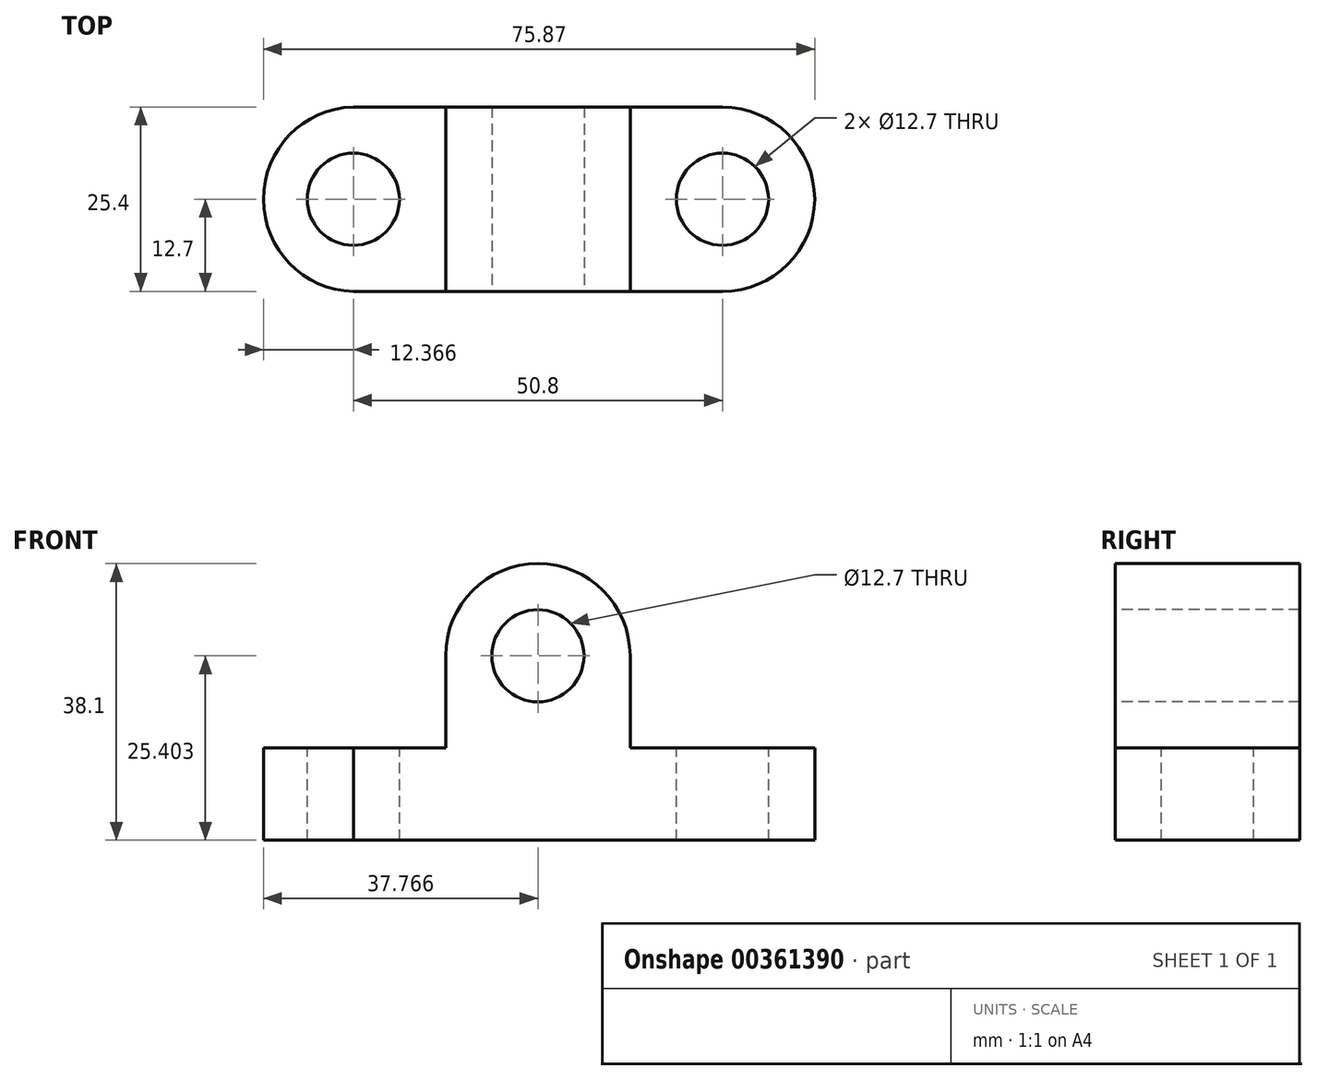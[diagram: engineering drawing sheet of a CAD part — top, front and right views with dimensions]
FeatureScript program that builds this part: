
annotation { "Feature Type Name" : "Feature", "Feature Type Description" : "" }
export const myFeature = defineFeature(function(context is Context, id is Id, definition is map)
    precondition{}
    {
        {
            var Q0;
            Q0=qCreatedBy(makeId("Front.planeOp"),FACE);
            var sketch = newSketch(context, id + "F0", { "sketchPlane" : qUnion([Q0])});
            skLineSegment(sketch, "E0", {"start": v(-39.1, 16.45) * mm, "end": v(-39.1, 3.75) * mm});
            skLineSegment(sketch, "E1", {"start": v(-39.1, 3.75) * mm, "end": v(37.1, 3.75) * mm});
            skLineSegment(sketch, "E2", {"start": v(37.1, 3.75) * mm, "end": v(37.1, 16.45) * mm});
            skLineSegment(sketch, "E3", {"start": v(37.1, 16.45) * mm, "end": v(11.7, 16.45) * mm});
            skLineSegment(sketch, "E4", {"start": v(11.7, 16.45) * mm, "end": v(11.7, 41.85) * mm});
            skLineSegment(sketch, "E5", {"start": v(11.7, 41.85) * mm, "end": v(-13.7, 41.85) * mm});
            skLineSegment(sketch, "E6", {"start": v(-13.7, 41.85) * mm, "end": v(-13.7, 16.45) * mm});
            skLineSegment(sketch, "E7", {"start": v(-13.7, 16.45) * mm, "end": v(-39.1, 16.45) * mm});
            skSolve(sketch);
        }
        {
            var Q0;
            Q0 = qSketchRegion(id + "F0", true);
            extrude(context, id + "F1", {"entities" : qUnion([Q0]), "depth" : 25.4 * mm});
        }
        {
            var Q0;
            Q0=makeQuery(id+"F1.opExtrude","CAP_FACE",FACE,{"disambiguationData":[OSD([sQuery(id+"F0.wireOp",EDGE,"E0"),sQuery(id+"F0.wireOp",EDGE,"E1"),sQuery(id+"F0.wireOp",EDGE,"E2"),sQuery(id+"F0.wireOp",EDGE,"E3"),sQuery(id+"F0.wireOp",EDGE,"E4"),sQuery(id+"F0.wireOp",EDGE,"E5"),sQuery(id+"F0.wireOp",EDGE,"E6"),sQuery(id+"F0.wireOp",EDGE,"E7")])],"isStart":false});
            var sketch = newSketch(context, id + "F2", { "sketchPlane" : qUnion([Q0])});
            skArc(sketch, "E8", {"start": v(11.7, 29.15) * mm, "mid": v(-1, 41.85) * mm, "end": v(-13.7, 29.15) * mm});
            skCircle(sketch, "E9", {"center": v(-1, 29.15) * mm, "radius": 6.35 * mm});
            skSolve(sketch);
        }
        {
            var Q0;
            Q0 = qSketchRegion(id + "F2", true);
            var Q1;
            {var subQ0=sQuery(id+"F2.wireOp",EDGE,"E8");var subQ1=makeQuery(id+"F1.opExtrude","CAP_EDGE",EDGE,{"disambiguationData":[OSD([sQuery(id+"F0.wireOp",EDGE,"E6")])],"isStart":false});var subQ2=makeQuery(id+"F2.imprint","INTERSECT",VERTEX,{"derivedFrom":[subQ1,subQ0]});Q1=makeQuery(id+"F2.imprint","IMPRINT",FACE,{"disambiguationData":[TD([[makeQuery(id+"F2.imprint","IMPRINT",EDGE,{"disambiguationData":[TD([[subQ2,1.0]])],"derivedFrom":subQ0}),-1.0]])]});}
            var Q2;
            {var subQ0=sQuery(id+"F2.wireOp",EDGE,"E8");var subQ1=makeQuery(id+"F1.opExtrude","CAP_EDGE",EDGE,{"disambiguationData":[OSD([sQuery(id+"F0.wireOp",EDGE,"E4")])],"isStart":false});var subQ2=makeQuery(id+"F2.imprint","INTERSECT",VERTEX,{"derivedFrom":[subQ1,subQ0]});Q2=makeQuery(id+"F2.imprint","IMPRINT",FACE,{"disambiguationData":[TD([[makeQuery(id+"F2.imprint","IMPRINT",EDGE,{"disambiguationData":[TD([[subQ2,-1.0]])],"derivedFrom":subQ0}),-1.0]])]});}
            extrude(context, id + "F3", {"entities" : qUnion([Q0, Q1, Q2]), "operationType" : NewBodyOperationType.REMOVE, "oppositeDirection" : true, "depth" : 25.4 * mm});
        }
        {
            var Q0;
            Q0=makeQuery(id+"F1.opExtrude","SWEPT_FACE",FACE,{"disambiguationData":[OSD([sQuery(id+"F0.wireOp",EDGE,"E7")])]});
            var sketch = newSketch(context, id + "F4", { "sketchPlane" : qUnion([Q0])});
            skCircle(sketch, "E10", {"center": v(-26.4, -12.7) * mm, "radius": 6.35 * mm});
            skArc(sketch, "E11", {"start": v(-26.4, 0) * mm, "mid": v(-38.76, -12.7) * mm, "end": v(-26.4, -25.4) * mm});
            skSolve(sketch);
        }
        {
            var Q0;
            Q0 = qSketchRegion(id + "F4", true);
            var Q1;
            {var subQ0=sQuery(id+"F4.wireOp",EDGE,"E11");Q1=makeQuery(id+"F4.imprint","IMPRINT",FACE,{"disambiguationData":[TD([[makeQuery(id+"F4.imprint","IMPRINT",EDGE,{"derivedFrom":subQ0}),-1.0]])]});}
            extrude(context, id + "F5", {"entities" : qUnion([Q0, Q1]), "operationType" : NewBodyOperationType.REMOVE, "oppositeDirection" : true, "depth" : 25.4 * mm});
        }
        {
            var Q0;
            Q0=makeQuery(id+"F1.opExtrude","SWEPT_FACE",FACE,{"disambiguationData":[OSD([sQuery(id+"F0.wireOp",EDGE,"E3")])]});
            var sketch = newSketch(context, id + "F6", { "sketchPlane" : qUnion([Q0])});
            skCircle(sketch, "E12", {"center": v(24.4, -12.7) * mm, "radius": 6.35 * mm});
            skArc(sketch, "E13", {"start": v(24.4, -25.4) * mm, "mid": v(37.1, -12.7) * mm, "end": v(24.4, 0) * mm});
            skSolve(sketch);
        }
        {
            var Q0;
            Q0 = qSketchRegion(id + "F6", true);
            var Q1;
            {var subQ0=sQuery(id+"F6.wireOp",EDGE,"E13");var subQ1=sQuery(id+"F0.wireOp",EDGE,"E3");var subQ2=makeQuery(id+"F1.opExtrude","CAP_EDGE",EDGE,{"disambiguationData":[OSD([subQ1])],"isStart":true});var subQ3=makeQuery(id+"F6.imprint","INTERSECT",VERTEX,{"derivedFrom":[subQ2,subQ0]});Q1=makeQuery(id+"F6.imprint","IMPRINT",FACE,{"disambiguationData":[TD([[makeQuery(id+"F6.imprint","IMPRINT",EDGE,{"disambiguationData":[TD([[subQ3,1.0]])],"derivedFrom":subQ0}),-1.0]])]});}
            var Q2;
            {var subQ0=sQuery(id+"F6.wireOp",EDGE,"E13");var subQ1=sQuery(id+"F0.wireOp",EDGE,"E3");var subQ2=makeQuery(id+"F1.opExtrude","CAP_EDGE",EDGE,{"disambiguationData":[OSD([subQ1])],"isStart":false});var subQ3=makeQuery(id+"F6.imprint","INTERSECT",VERTEX,{"derivedFrom":[subQ2,subQ0]});Q2=makeQuery(id+"F6.imprint","IMPRINT",FACE,{"disambiguationData":[TD([[makeQuery(id+"F6.imprint","IMPRINT",EDGE,{"disambiguationData":[TD([[subQ3,-1.0]])],"derivedFrom":subQ0}),-1.0]])]});}
            extrude(context, id + "F7", {"entities" : qUnion([Q0, Q1, Q2]), "operationType" : NewBodyOperationType.REMOVE, "oppositeDirection" : true, "depth" : 25.4 * mm});
        }
    });
